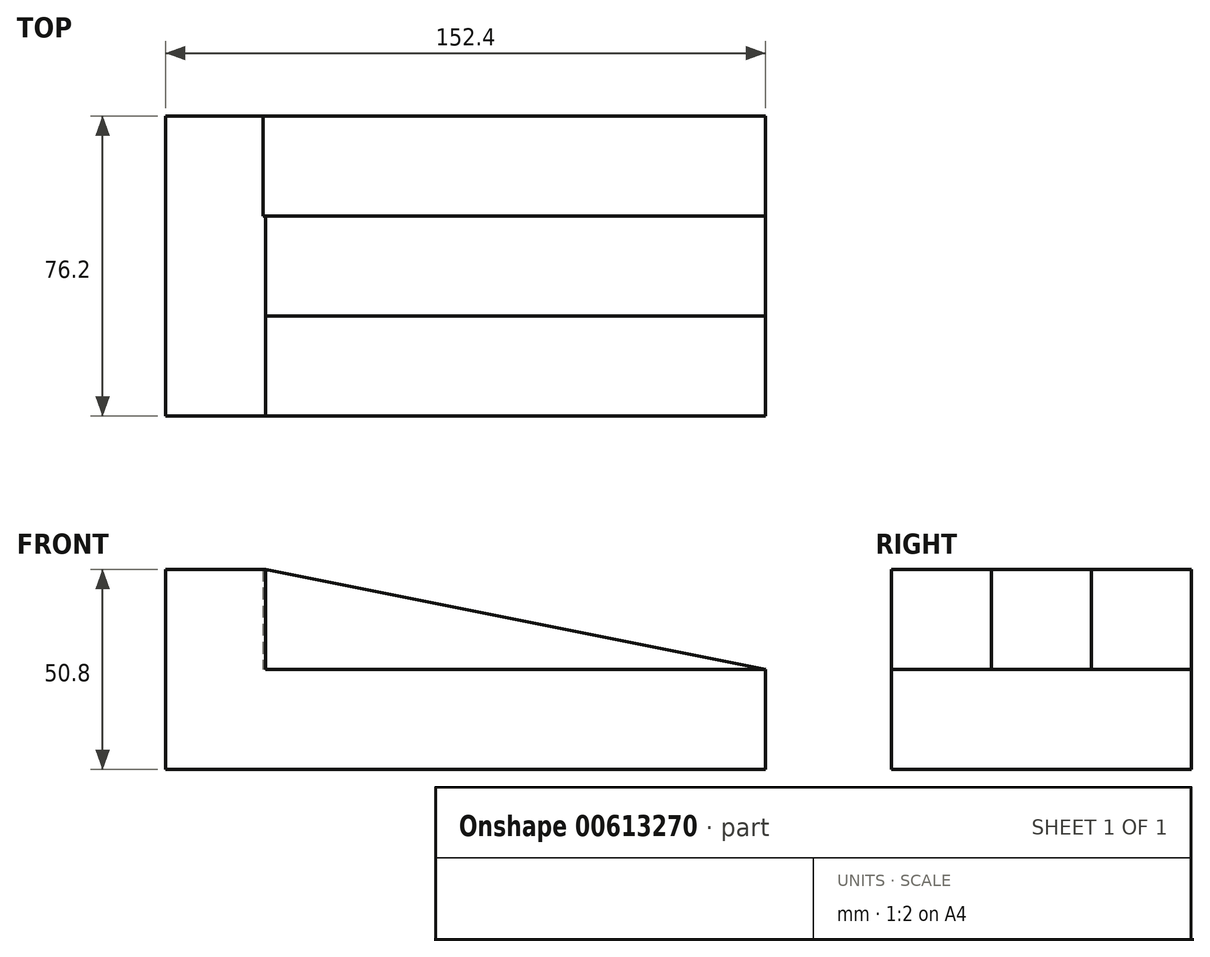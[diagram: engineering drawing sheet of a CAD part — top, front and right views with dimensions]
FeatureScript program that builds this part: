
annotation { "Feature Type Name" : "Feature", "Feature Type Description" : "" }
export const myFeature = defineFeature(function(context is Context, id is Id, definition is map)
    precondition{}
    {
        {
            var Q0;
            Q0=qCreatedBy(makeId("Front.planeOp"),FACE);
            var sketch = newSketch(context, id + "F0", { "sketchPlane" : qUnion([Q0])});
            skLineSegment(sketch, "E0.bottom", {"start": v(0, 0) * mm, "end": v(152.4, 0) * mm});
            skLineSegment(sketch, "E0.top", {"start": v(0, 50.8) * mm, "end": v(152.4, 50.8) * mm});
            skLineSegment(sketch, "E0.left", {"start": v(0, 0) * mm, "end": v(0, 50.8) * mm});
            skLineSegment(sketch, "E0.right", {"start": v(152.4, 0) * mm, "end": v(152.4, 50.8) * mm});
            skSolve(sketch);
        }
        {
            var Q0;
            Q0 = qSketchRegion(id + "F0", true);
            extrude(context, id + "F1", {"entities" : qUnion([Q0]), "depth" : 76.2 * mm, "offsetDistance" : 25.4 * mm});
        }
        {
            var Q0;
            Q0=makeQuery(id+"F1.opExtrude","CAP_FACE",FACE,{"disambiguationData":[OSD([sQuery(id+"F0.wireOp",EDGE,"E0.bottom"),sQuery(id+"F0.wireOp",EDGE,"E0.top"),sQuery(id+"F0.wireOp",EDGE,"E0.left"),sQuery(id+"F0.wireOp",EDGE,"E0.right")])],"isStart":false});
            var sketch = newSketch(context, id + "F2", { "sketchPlane" : qUnion([Q0])});
            skLineSegment(sketch, "E1", {"start": v(152.4, 0) * mm, "end": v(152.4, 25.4) * mm});
            skLineSegment(sketch, "E2", {"start": v(0, 50.8) * mm, "end": v(25.4, 50.8) * mm});
            skLineSegment(sketch, "E3", {"start": v(25.4, 50.8) * mm, "end": v(25.4, 25.4) * mm});
            skLineSegment(sketch, "E4", {"start": v(25.4, 25.4) * mm, "end": v(152.4, 25.4) * mm});
            skSolve(sketch);
        }
        {
            var Q0;
            {var subQ0=sQuery(id+"F2.wireOp",EDGE,"E3");Q0=makeQuery(id+"F2.imprint","IMPRINT",FACE,{"disambiguationData":[TD([[makeQuery(id+"F2.imprint","IMPRINT",EDGE,{"derivedFrom":subQ0}),1.0]])]});}
            extrude(context, id + "F3", {"entities" : qUnion([Q0]), "operationType" : NewBodyOperationType.REMOVE, "oppositeDirection" : true, "depth" : 25.4 * mm, "offsetDistance" : 25.4 * mm});
        }
        {
            var Q0;
            Q0=makeQuery(id+"F1.opExtrude","CAP_FACE",FACE,{"disambiguationData":[OSD([sQuery(id+"F0.wireOp",EDGE,"E0.bottom"),sQuery(id+"F0.wireOp",EDGE,"E0.top"),sQuery(id+"F0.wireOp",EDGE,"E0.left"),sQuery(id+"F0.wireOp",EDGE,"E0.right")])],"isStart":true});
            var sketch = newSketch(context, id + "F4", { "sketchPlane" : qUnion([Q0])});
            skLineSegment(sketch, "E5", {"start": v(-24.77, 50.8) * mm, "end": v(-24.77, 25.4) * mm});
            skLineSegment(sketch, "E6", {"start": v(-152.4, 0) * mm, "end": v(-152.4, 25.4) * mm});
            skLineSegment(sketch, "E7", {"start": v(-152.4, 25.4) * mm, "end": v(-24.77, 25.4) * mm});
            skSolve(sketch);
        }
        {
            var Q0;
            {var subQ0=sQuery(id+"F4.wireOp",EDGE,"E5");Q0=makeQuery(id+"F4.imprint","IMPRINT",FACE,{"disambiguationData":[TD([[makeQuery(id+"F4.imprint","IMPRINT",EDGE,{"derivedFrom":subQ0}),-1.0]])]});}
            extrude(context, id + "F5", {"entities" : qUnion([Q0]), "operationType" : NewBodyOperationType.REMOVE, "oppositeDirection" : true, "depth" : 25.4 * mm, "offsetDistance" : 25.4 * mm});
        }
        {
            var Q0;
            Q0=makeQuery(id+"F3.boolean.opBoolean","COPY",FACE,{"derivedFrom":makeQuery(id+"F3.opExtrude","CAP_FACE",FACE,{"disambiguationData":[OSD([sQuery(id+"F0.wireOp",EDGE,"E0.top"),sQuery(id+"F0.wireOp",EDGE,"E0.right"),sQuery(id+"F2.wireOp",EDGE,"E3"),sQuery(id+"F2.wireOp",EDGE,"E4")])],"isStart":false})});
            var sketch = newSketch(context, id + "F6", { "sketchPlane" : qUnion([Q0])});
            skLineSegment(sketch, "E8", {"start": v(25.4, 50.8) * mm, "end": v(152.4, 25.4) * mm});
            skSolve(sketch);
        }
        {
            var Q0;
            Q0 = qSketchRegion(id + "F6", true);
            var Q1;
            Q1=makeQuery(id+"F6.imprint","IMPRINT",FACE,{"disambiguationData":[TD([[makeQuery(id+"F6.imprint","IMPRINT",EDGE,{"derivedFrom":sQuery(id+"F6.wireOp",EDGE,"E8")}),1.0]])]});
            extrude(context, id + "F7", {"entities" : qUnion([Q0, Q1]), "operationType" : NewBodyOperationType.REMOVE, "oppositeDirection" : true, "depth" : 25.4 * mm, "offsetDistance" : 25.4 * mm});
        }
    });
